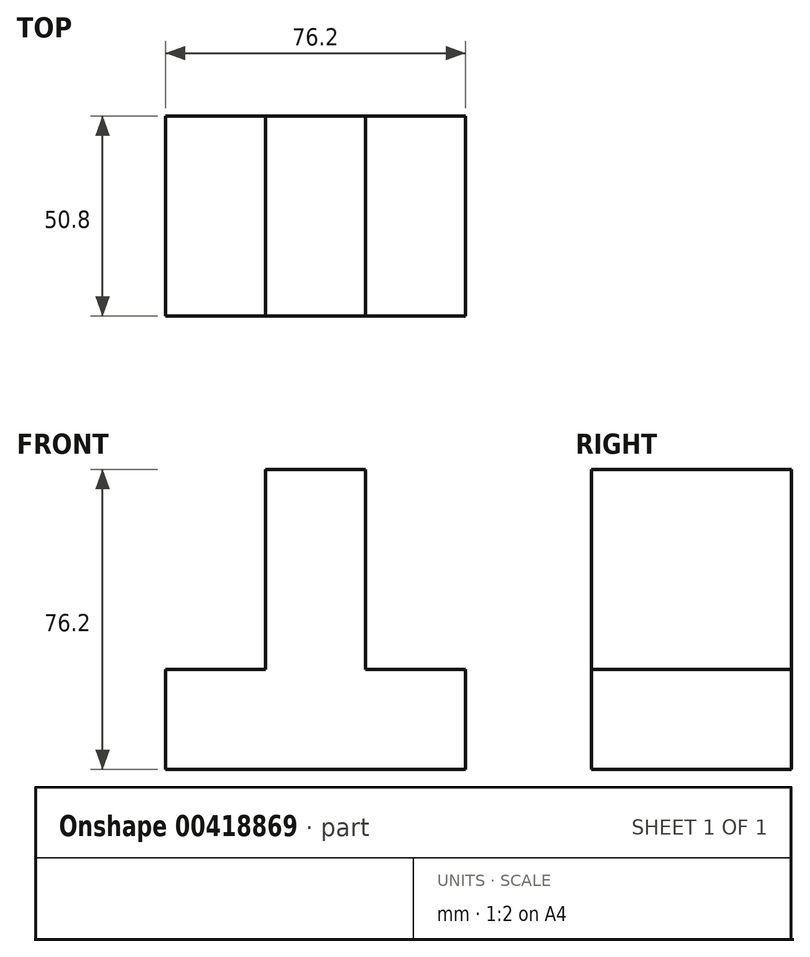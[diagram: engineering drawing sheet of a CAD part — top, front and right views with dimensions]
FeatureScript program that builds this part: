
annotation { "Feature Type Name" : "Feature", "Feature Type Description" : "" }
export const myFeature = defineFeature(function(context is Context, id is Id, definition is map)
    precondition{}
    {
        {
            var Q0;
            Q0=qCreatedBy(makeId("Front.planeOp"),FACE);
            var sketch = newSketch(context, id + "F0", { "sketchPlane" : qUnion([Q0])});
            skLineSegment(sketch, "E0", {"start": v(0, 0) * mm, "end": v(0, 25.4) * mm});
            skLineSegment(sketch, "E1", {"start": v(0, 0) * mm, "end": v(-76.2, 0) * mm});
            skLineSegment(sketch, "E2", {"start": v(-76.2, 0) * mm, "end": v(-76.2, 25.4) * mm});
            skLineSegment(sketch, "E3", {"start": v(-76.2, 25.4) * mm, "end": v(-50.8, 25.4) * mm});
            skLineSegment(sketch, "E4", {"start": v(0, 25.4) * mm, "end": v(-25.4, 25.4) * mm});
            skLineSegment(sketch, "E5", {"start": v(-50.8, 25.4) * mm, "end": v(-50.8, 76.2) * mm});
            skLineSegment(sketch, "E6", {"start": v(-50.8, 76.2) * mm, "end": v(-25.4, 76.2) * mm});
            skLineSegment(sketch, "E7", {"start": v(-25.4, 25.4) * mm, "end": v(-25.4, 76.2) * mm});
            skSolve(sketch);
        }
        {
            var Q0;
            Q0 = qSketchRegion(id + "F0", true);
            extrude(context, id + "F1", {"entities" : qUnion([Q0]), "depth" : 50.8 * mm});
        }
    });
